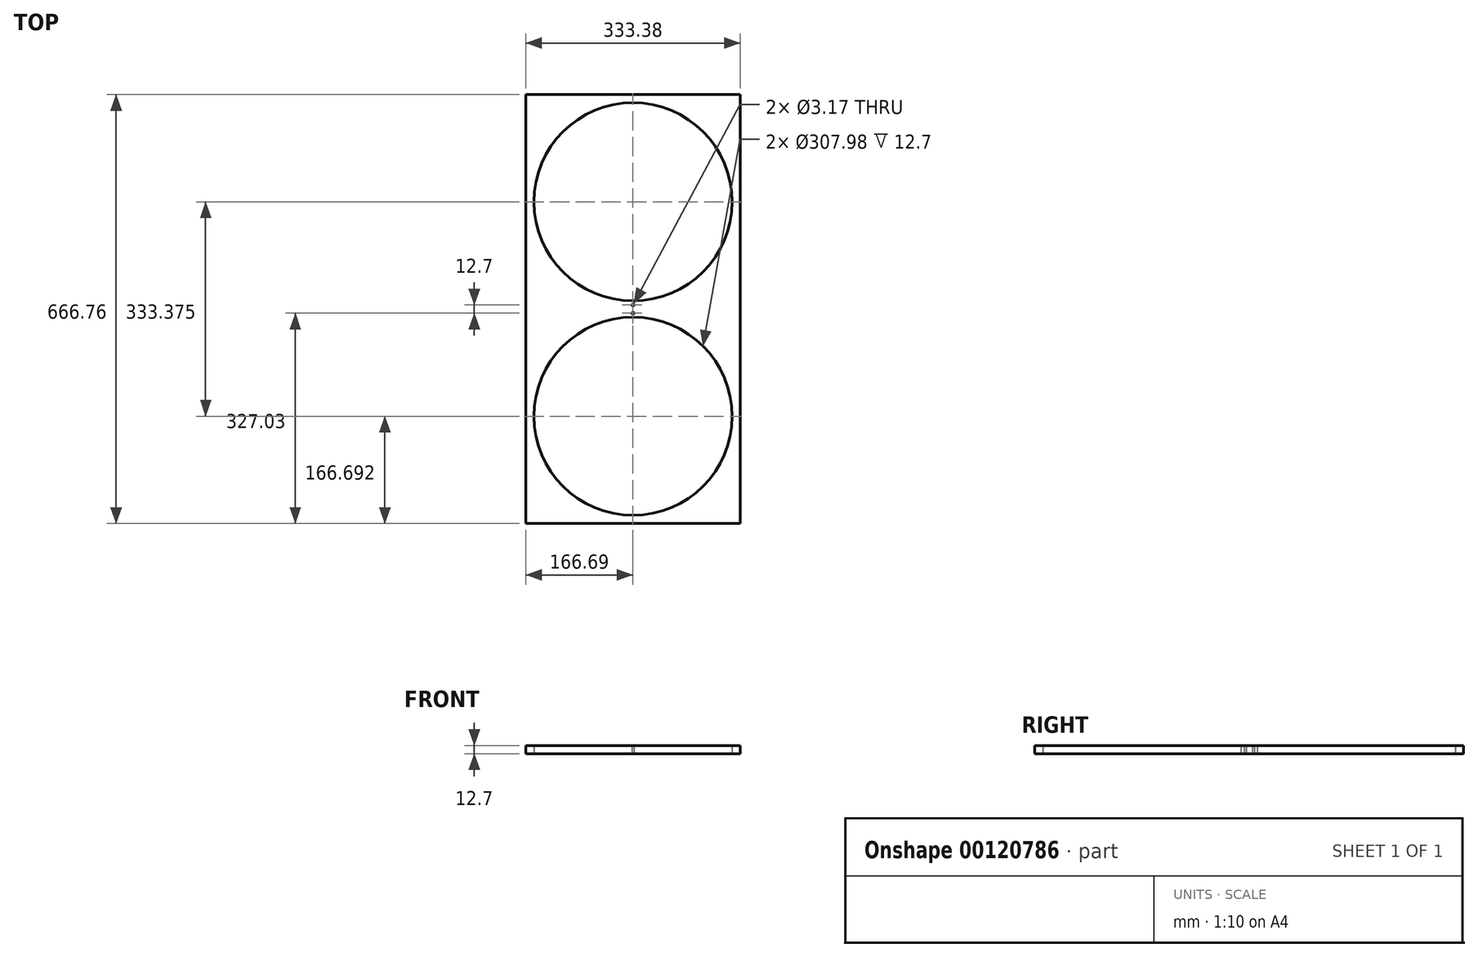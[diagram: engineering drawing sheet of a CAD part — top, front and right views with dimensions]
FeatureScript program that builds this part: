
annotation { "Feature Type Name" : "Feature", "Feature Type Description" : "" }
export const myFeature = defineFeature(function(context is Context, id is Id, definition is map)
    precondition{}
    {
        {
            var Q0;
            Q0=qCreatedBy(makeId("Top.planeOp"),FACE);
            var sketch = newSketch(context, id + "F0", { "sketchPlane" : qUnion([Q0])});
            skLineSegment(sketch, "E0.bottom", {"start": v(166.69, -166.69) * mm, "end": v(-166.69, -166.69) * mm});
            skLineSegment(sketch, "E0.top", {"start": v(166.69, 166.69) * mm, "end": v(-166.69, 166.69) * mm});
            skLineSegment(sketch, "E0.left", {"start": v(166.69, -166.69) * mm, "end": v(166.69, 166.69) * mm});
            skLineSegment(sketch, "E0.right", {"start": v(-166.69, -166.69) * mm, "end": v(-166.69, 166.69) * mm});
            skPoint(sketch, "E0.middle", {"position": v(0, 0) * mm});
            skCircle(sketch, "E1", {"center": v(0, -166.69) * mm, "radius": 166.69 * mm});
            skCircle(sketch, "E2", {"center": v(0, 166.69) * mm, "radius": 166.69 * mm});
            skCircle(sketch, "E3", {"center": v(0, -166.69) * mm, "radius": 153.99 * mm});
            skCircle(sketch, "E4", {"center": v(0, 166.69) * mm, "radius": 153.99 * mm});
            skLineSegment(sketch, "E5.bottom", {"start": v(-166.69, 333.38) * mm, "end": v(166.69, 333.38) * mm});
            skLineSegment(sketch, "E5.top", {"start": v(-166.69, -333.38) * mm, "end": v(166.69, -333.38) * mm});
            skLineSegment(sketch, "E5.left", {"start": v(-166.69, 333.38) * mm, "end": v(-166.69, -333.38) * mm});
            skLineSegment(sketch, "E5.right", {"start": v(166.69, 333.38) * mm, "end": v(166.69, -333.38) * mm});
            skLineSegment(sketch, "E6", {"start": v(0, 0) * mm, "end": v(0, -12.7) * mm});
            skCircle(sketch, "E7", {"center": v(0, -6.35) * mm, "radius": 1.59 * mm});
            skCircle(sketch, "E8.MirrorC", {"center": v(0, 6.35) * mm, "radius": 1.59 * mm});
            skSolve(sketch);
        }
        {
            var Q0;
            {var subQ1=sQuery(id+"F0.wireOp",EDGE,"E0.bottom");var subQ3=sQuery(id+"F0.wireOp",EDGE,"E3");var subQ4=makeQuery(id+"F0.imprint","INTERSECT",VERTEX,{"disambiguationData":[OD(0.0)],"derivedFrom":[subQ1,subQ3]});Q0=makeQuery(id+"F0.imprint","IMPRINT",FACE,{"disambiguationData":[TD([[makeQuery(id+"F0.imprint","IMPRINT",EDGE,{"disambiguationData":[TD([[subQ4,1.0]])],"derivedFrom":subQ3}),-1.0]])]});}
            var Q1;
            {var subQ1=sQuery(id+"F0.wireOp",EDGE,"E0.top");var subQ3=sQuery(id+"F0.wireOp",EDGE,"E4");var subQ4=makeQuery(id+"F0.imprint","INTERSECT",VERTEX,{"disambiguationData":[OD(0.0)],"derivedFrom":[subQ1,subQ3]});Q1=makeQuery(id+"F0.imprint","IMPRINT",FACE,{"disambiguationData":[TD([[makeQuery(id+"F0.imprint","IMPRINT",EDGE,{"disambiguationData":[TD([[subQ4,-1.0]])],"derivedFrom":subQ3}),-1.0]])]});}
            var Q2;
            {var subQ0=sQuery(id+"F0.wireOp",EDGE,"E0.right");Q2=makeQuery(id+"F0.imprint","IMPRINT",FACE,{"disambiguationData":[TD([[makeQuery(id+"F0.imprint","IMPRINT",EDGE,{"derivedFrom":subQ0}),-1.0]])]});}
            var Q3;
            {var subQ1=sQuery(id+"F0.wireOp",EDGE,"E0.bottom");var subQ4=sQuery(id+"F0.wireOp",EDGE,"E3");var subQ7=makeQuery(id+"F0.imprint","INTERSECT",VERTEX,{"disambiguationData":[OD(0.0)],"derivedFrom":[subQ1,subQ4]});Q3=makeQuery(id+"F0.imprint","IMPRINT",FACE,{"disambiguationData":[TD([[makeQuery(id+"F0.imprint","IMPRINT",EDGE,{"disambiguationData":[TD([[subQ7,-1.0]])],"derivedFrom":subQ4}),-1.0]])]});}
            var Q4;
            {var subQ1=sQuery(id+"F0.wireOp",EDGE,"E0.top");var subQ4=sQuery(id+"F0.wireOp",EDGE,"E4");var subQ5=makeQuery(id+"F0.imprint","INTERSECT",VERTEX,{"disambiguationData":[OD(0.0)],"derivedFrom":[subQ1,subQ4]});Q4=makeQuery(id+"F0.imprint","IMPRINT",FACE,{"disambiguationData":[TD([[makeQuery(id+"F0.imprint","IMPRINT",EDGE,{"disambiguationData":[TD([[subQ5,1.0]])],"derivedFrom":subQ4}),-1.0]])]});}
            var Q5;
            {var subQ0=sQuery(id+"F0.wireOp",EDGE,"E0.left");Q5=makeQuery(id+"F0.imprint","IMPRINT",FACE,{"disambiguationData":[TD([[makeQuery(id+"F0.imprint","IMPRINT",EDGE,{"derivedFrom":subQ0}),1.0]])]});}
            var Q6;
            {var subQ1=sQuery(id+"F0.wireOp",EDGE,"E1");var subQ3=sQuery(id+"F0.wireOp",EDGE,"E2");var subQ4=makeQuery(id+"F0.imprint","INTERSECT",VERTEX,{"derivedFrom":[subQ1,subQ3]});Q6=makeQuery(id+"F0.imprint","IMPRINT",FACE,{"disambiguationData":[TD([[makeQuery(id+"F0.imprint","IMPRINT",EDGE,{"disambiguationData":[TD([[subQ4,1.0]])],"derivedFrom":subQ1}),-1.0]])]});}
            var Q7;
            {var subQ1=sQuery(id+"F0.wireOp",EDGE,"E1");var subQ3=sQuery(id+"F0.wireOp",EDGE,"E2");var subQ4=makeQuery(id+"F0.imprint","INTERSECT",VERTEX,{"derivedFrom":[subQ1,subQ3]});Q7=makeQuery(id+"F0.imprint","IMPRINT",FACE,{"disambiguationData":[TD([[makeQuery(id+"F0.imprint","IMPRINT",EDGE,{"disambiguationData":[TD([[subQ4,-1.0]])],"derivedFrom":subQ1}),-1.0]])]});}
            var Q8;
            {var subQ0=sQuery(id+"F0.wireOp",EDGE,"E5.left");var subQ3=sQuery(id+"F0.wireOp",EDGE,"E5.top");var subQ5=makeQuery(id+"F0.imprint","INTERSECT",VERTEX,{"derivedFrom":[subQ3,subQ0]});Q8=makeQuery(id+"F0.imprint","IMPRINT",FACE,{"disambiguationData":[TD([[makeQuery(id+"F0.imprint","IMPRINT",EDGE,{"disambiguationData":[TD([[subQ5,-1.0]])],"derivedFrom":subQ3}),1.0]])]});}
            var Q9;
            {var subQ0=sQuery(id+"F0.wireOp",EDGE,"E5.right");var subQ3=sQuery(id+"F0.wireOp",EDGE,"E5.top");var subQ5=makeQuery(id+"F0.imprint","INTERSECT",VERTEX,{"derivedFrom":[subQ3,subQ0]});Q9=makeQuery(id+"F0.imprint","IMPRINT",FACE,{"disambiguationData":[TD([[makeQuery(id+"F0.imprint","IMPRINT",EDGE,{"disambiguationData":[TD([[subQ5,1.0]])],"derivedFrom":subQ3}),1.0]])]});}
            var Q10;
            {var subQ0=sQuery(id+"F0.wireOp",EDGE,"E5.left");var subQ3=sQuery(id+"F0.wireOp",EDGE,"E5.bottom");var subQ5=makeQuery(id+"F0.imprint","INTERSECT",VERTEX,{"derivedFrom":[subQ3,subQ0]});Q10=makeQuery(id+"F0.imprint","IMPRINT",FACE,{"disambiguationData":[TD([[makeQuery(id+"F0.imprint","IMPRINT",EDGE,{"disambiguationData":[TD([[subQ5,-1.0]])],"derivedFrom":subQ3}),-1.0]])]});}
            var Q11;
            {var subQ0=sQuery(id+"F0.wireOp",EDGE,"E5.right");var subQ3=sQuery(id+"F0.wireOp",EDGE,"E5.bottom");var subQ5=makeQuery(id+"F0.imprint","INTERSECT",VERTEX,{"derivedFrom":[subQ3,subQ0]});Q11=makeQuery(id+"F0.imprint","IMPRINT",FACE,{"disambiguationData":[TD([[makeQuery(id+"F0.imprint","IMPRINT",EDGE,{"disambiguationData":[TD([[subQ5,1.0]])],"derivedFrom":subQ3}),-1.0]])]});}
            var Q12;
            {var subQ0=sQuery(id+"F0.wireOp",EDGE,"E6");var subQ7=sQuery(id+"F0.wireOp",EDGE,"E3");var subQ9=makeQuery(id+"F0.imprint","INTERSECT",VERTEX,{"derivedFrom":[subQ7,subQ0]});Q12=makeQuery(id+"F0.imprint","IMPRINT",FACE,{"disambiguationData":[TD([[makeQuery(id+"F0.imprint","IMPRINT",EDGE,{"disambiguationData":[TD([[subQ9,-1.0]])],"derivedFrom":subQ7}),-1.0]])]});}
            extrude(context, id + "F1", {"entities" : qUnion([Q0, Q1, Q2, Q3, Q4, Q5, Q6, Q7, Q8, Q9, Q10, Q11, Q12]), "depth" : 12.7 * mm});
        }
    });
